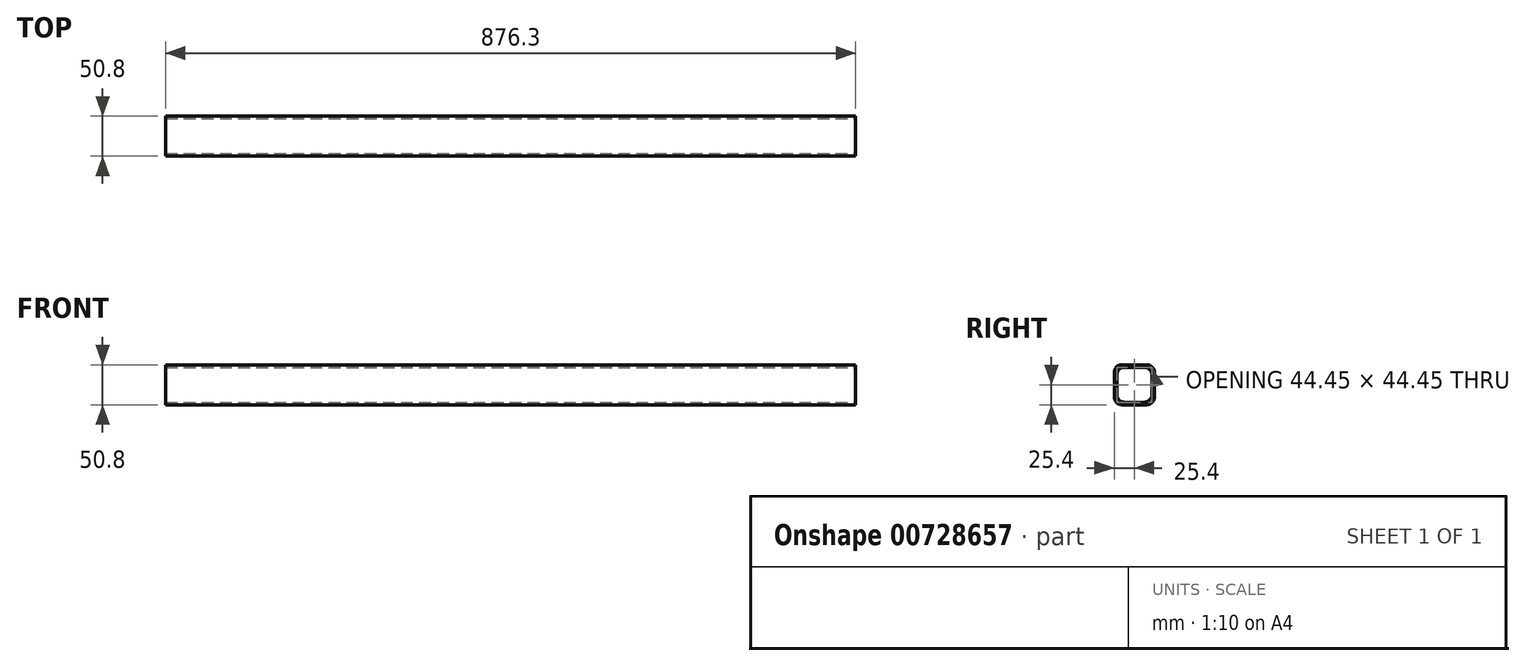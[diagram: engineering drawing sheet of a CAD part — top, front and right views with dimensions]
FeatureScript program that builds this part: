
annotation { "Feature Type Name" : "Feature", "Feature Type Description" : "" }
export const myFeature = defineFeature(function(context is Context, id is Id, definition is map)
    precondition{}
    {
        {
            var Q0;
            Q0=qCreatedBy(makeId("Right.planeOp"),FACE);
            var sketch = newSketch(context, id + "F0", { "sketchPlane" : qUnion([Q0])});
            skLineSegment(sketch, "E0.bottom", {"start": v(0, 0) * mm, "end": v(50.8, 0) * mm});
            skLineSegment(sketch, "E0.top", {"start": v(0, 50.8) * mm, "end": v(50.8, 50.8) * mm});
            skLineSegment(sketch, "E0.left", {"start": v(0, 0) * mm, "end": v(0, 50.8) * mm});
            skLineSegment(sketch, "E0.right", {"start": v(50.8, 0) * mm, "end": v(50.8, 50.8) * mm});
            skSolve(sketch);
        }
        {
            var Q0;
            Q0 = qSketchRegion(id + "F0", true);
            extrude(context, id + "F1", {"entities" : qUnion([Q0]), "oppositeDirection" : true, "depth" : 876.3 * mm, "offsetDistance" : 25.4 * mm});
        }
        {
            var Q0;
            Q0=makeQuery(id+"F1.opExtrude","CAP_FACE",FACE,{"disambiguationData":[OSD([sQuery(id+"F0.wireOp",EDGE,"E0.bottom"),sQuery(id+"F0.wireOp",EDGE,"E0.top"),sQuery(id+"F0.wireOp",EDGE,"E0.left"),sQuery(id+"F0.wireOp",EDGE,"E0.right")])],"isStart":true});
            var sketch = newSketch(context, id + "F2", { "sketchPlane" : qUnion([Q0])});
            skLineSegment(sketch, "E1.0", {"start": v(3.17, 47.63) * mm, "end": v(47.63, 47.63) * mm});
            skLineSegment(sketch, "E1.1", {"start": v(3.17, 3.17) * mm, "end": v(3.17, 47.63) * mm});
            skLineSegment(sketch, "E1.2", {"start": v(3.17, 3.17) * mm, "end": v(47.63, 3.17) * mm});
            skLineSegment(sketch, "E1.3", {"start": v(47.63, 3.17) * mm, "end": v(47.63, 47.63) * mm});
            skSolve(sketch);
        }
        {
            var Q0;
            Q0 = qSketchRegion(id + "F2", true);
            extrude(context, id + "F3", {"entities" : qUnion([Q0]), "operationType" : NewBodyOperationType.REMOVE, "oppositeDirection" : true, "depth" : 876.3 * mm, "offsetDistance" : 25.4 * mm});
        }
        {
            var Q0;
            Q0=makeQuery(id+"F3.boolean.opBoolean","COPY",EDGE,{"derivedFrom":makeQuery(id+"F3.opExtrude","SWEPT_EDGE",EDGE,{"disambiguationData":[OSD([sQuery(id+"F2.wireOp",EDGE,"E1.1"),sQuery(id+"F2.wireOp",EDGE,"E1.2")])]})});
            var Q1;
            Q1=makeQuery(id+"F3.boolean.opBoolean","COPY",EDGE,{"derivedFrom":makeQuery(id+"F3.opExtrude","SWEPT_EDGE",EDGE,{"disambiguationData":[OSD([sQuery(id+"F2.wireOp",EDGE,"E1.2"),sQuery(id+"F2.wireOp",EDGE,"E1.3")])]})});
            var Q2;
            Q2=makeQuery(id+"F3.boolean.opBoolean","COPY",EDGE,{"derivedFrom":makeQuery(id+"F3.opExtrude","SWEPT_EDGE",EDGE,{"disambiguationData":[OSD([sQuery(id+"F2.wireOp",EDGE,"E1.0"),sQuery(id+"F2.wireOp",EDGE,"E1.3")])]})});
            var Q3;
            Q3=makeQuery(id+"F3.boolean.opBoolean","COPY",EDGE,{"derivedFrom":makeQuery(id+"F3.opExtrude","SWEPT_EDGE",EDGE,{"disambiguationData":[OSD([sQuery(id+"F2.wireOp",EDGE,"E1.0"),sQuery(id+"F2.wireOp",EDGE,"E1.1")])]})});
            var Q4;
            Q4=makeQuery(id+"F1.opExtrude","SWEPT_EDGE",EDGE,{"disambiguationData":[OSD([sQuery(id+"F0.wireOp",EDGE,"E0.bottom"),sQuery(id+"F0.wireOp",EDGE,"E0.right")])]});
            var Q5;
            Q5=makeQuery(id+"F1.opExtrude","SWEPT_EDGE",EDGE,{"disambiguationData":[OSD([sQuery(id+"F0.wireOp",EDGE,"E0.top"),sQuery(id+"F0.wireOp",EDGE,"E0.right")])]});
            var Q6;
            Q6=makeQuery(id+"F1.opExtrude","SWEPT_EDGE",EDGE,{"disambiguationData":[OSD([sQuery(id+"F0.wireOp",EDGE,"E0.top"),sQuery(id+"F0.wireOp",EDGE,"E0.left")])]});
            var Q7;
            Q7=makeQuery(id+"F1.opExtrude","SWEPT_EDGE",EDGE,{"disambiguationData":[OSD([sQuery(id+"F0.wireOp",EDGE,"E0.bottom"),sQuery(id+"F0.wireOp",EDGE,"E0.left")])]});
            fillet(context, id + "F4", {"entities" : qUnion([Q0, Q1, Q2, Q3, Q4, Q5, Q6, Q7]), "radius" : 9.52 * mm, "tangentPropagation" : true, "allowEdgeOverflow" : false});
        }
    });
